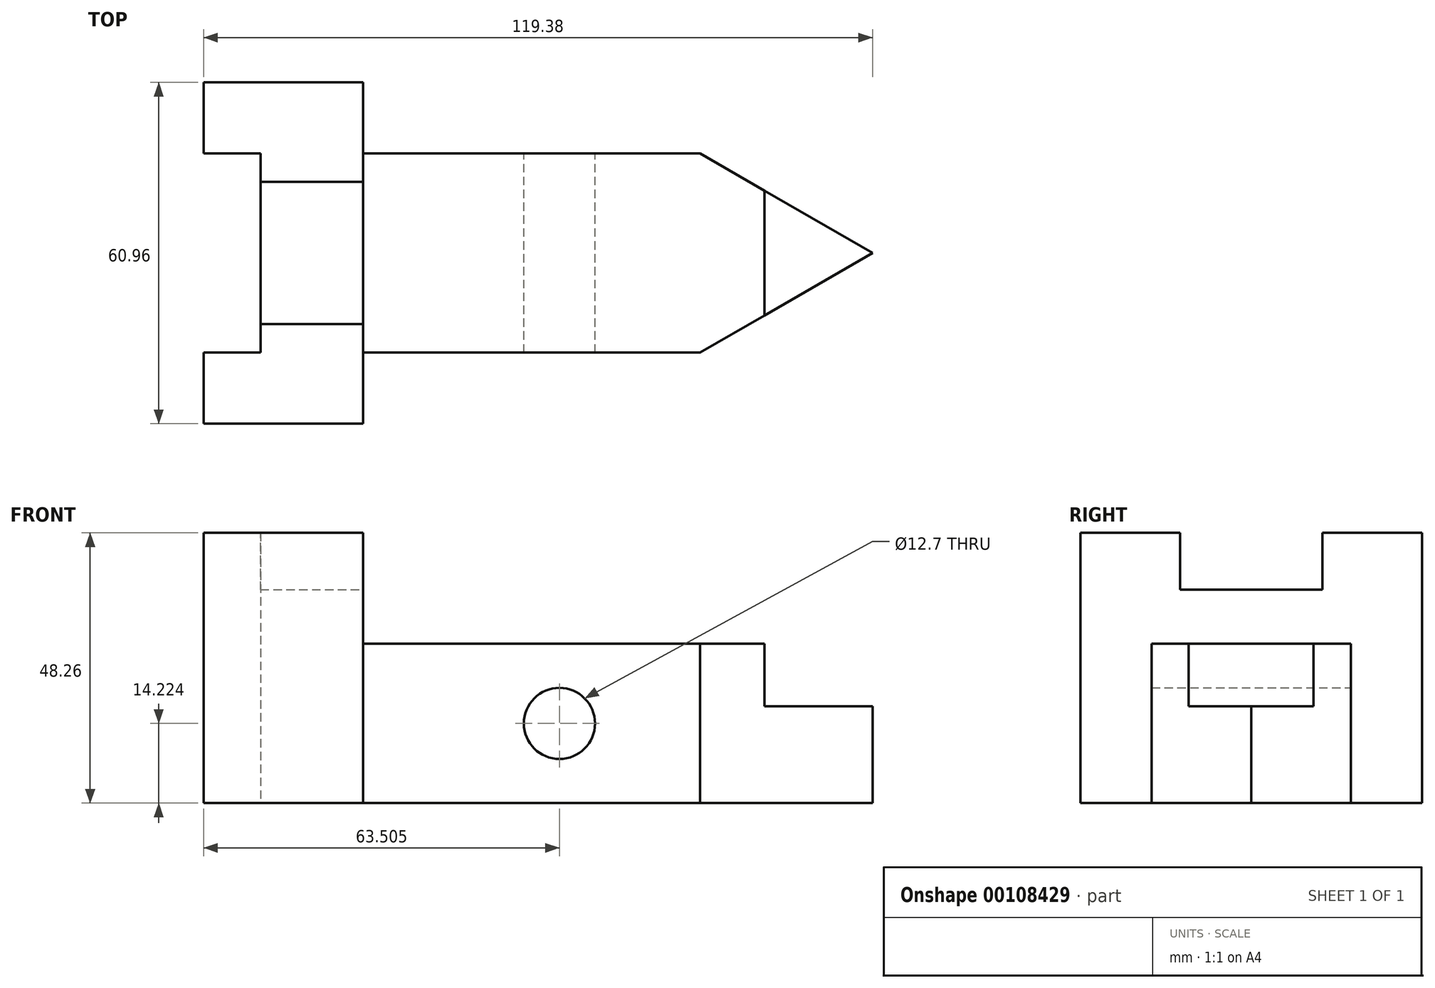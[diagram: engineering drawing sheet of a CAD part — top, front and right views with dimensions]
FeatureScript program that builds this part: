
annotation { "Feature Type Name" : "Feature", "Feature Type Description" : "" }
export const myFeature = defineFeature(function(context is Context, id is Id, definition is map)
    precondition{}
    {
        {
            var Q0;
            Q0=qCreatedBy(makeId("Top.planeOp"),FACE);
            var sketch = newSketch(context, id + "F0", { "sketchPlane" : qUnion([Q0])});
            skLineSegment(sketch, "E0.bottom", {"start": v(-33.19, 31.07) * mm, "end": v(-4.74, 31.07) * mm});
            skLineSegment(sketch, "E0.top", {"start": v(-33.19, -29.9) * mm, "end": v(-4.74, -29.9) * mm});
            skLineSegment(sketch, "E0.right", {"start": v(-4.74, 31.07) * mm, "end": v(-4.74, -29.9) * mm});
            skLineSegment(sketch, "E1", {"start": v(-33.19, 18.37) * mm, "end": v(-23.03, 18.37) * mm});
            skLineSegment(sketch, "E2", {"start": v(-23.03, 18.37) * mm, "end": v(-23.03, -17.2) * mm});
            skLineSegment(sketch, "E3", {"start": v(-23.03, -17.2) * mm, "end": v(-33.19, -17.2) * mm});
            skLineSegment(sketch, "E4", {"start": v(-33.19, 18.37) * mm, "end": v(-33.19, 31.07) * mm});
            skLineSegment(sketch, "E5", {"start": v(-33.19, -17.2) * mm, "end": v(-33.19, -29.9) * mm});
            skSolve(sketch);
        }
        {
            var Q0;
            Q0 = qSketchRegion(id + "F0", true);
            extrude(context, id + "F1", {"entities" : qUnion([Q0]), "depth" : 48.26 * mm});
        }
        {
            var Q0;
            Q0=makeQuery(id+"F1.opExtrude","CAP_FACE",FACE,{"disambiguationData":[OSD([sQuery(id+"F0.wireOp",EDGE,"E0.bottom"),sQuery(id+"F0.wireOp",EDGE,"E0.top"),sQuery(id+"F0.wireOp",EDGE,"E0.right"),sQuery(id+"F0.wireOp",EDGE,"E1"),sQuery(id+"F0.wireOp",EDGE,"E2"),sQuery(id+"F0.wireOp",EDGE,"E3"),sQuery(id+"F0.wireOp",EDGE,"E4"),sQuery(id+"F0.wireOp",EDGE,"E5")])],"isStart":false});
            var sketch = newSketch(context, id + "F2", { "sketchPlane" : qUnion([Q0])});
            skLineSegment(sketch, "E6", {"start": v(-23.03, 13.29) * mm, "end": v(-4.74, 13.29) * mm});
            skLineSegment(sketch, "E7", {"start": v(-4.74, 13.29) * mm, "end": v(-4.74, -12.11) * mm});
            skLineSegment(sketch, "E8", {"start": v(-4.74, -12.11) * mm, "end": v(-23.03, -12.11) * mm});
            skLineSegment(sketch, "E9", {"start": v(-23.03, -12.11) * mm, "end": v(-23.03, 13.29) * mm});
            skSolve(sketch);
        }
        {
            var Q0;
            Q0 = qSketchRegion(id + "F2", true);
            extrude(context, id + "F3", {"entities" : qUnion([Q0]), "operationType" : NewBodyOperationType.REMOVE, "oppositeDirection" : true, "depth" : 10.16 * mm});
        }
        {
            var Q0;
            Q0=qCreatedBy(makeId("Top.planeOp"),FACE);
            var sketch = newSketch(context, id + "F4", { "sketchPlane" : qUnion([Q0])});
            skLineSegment(sketch, "E10.bottom", {"start": v(-4.74, -17.2) * mm, "end": v(55.4, -17.2) * mm});
            skLineSegment(sketch, "E10.top", {"start": v(-4.74, 18.37) * mm, "end": v(55.4, 18.37) * mm});
            skLineSegment(sketch, "E10.left", {"start": v(-4.74, -17.2) * mm, "end": v(-4.74, 18.37) * mm});
            skLineSegment(sketch, "E11", {"start": v(55.4, 18.37) * mm, "end": v(86.2, 0.59) * mm});
            skLineSegment(sketch, "E12", {"start": v(86.2, 0.59) * mm, "end": v(55.4, -17.2) * mm});
            skSolve(sketch);
        }
        {
            var Q0;
            Q0 = qSketchRegion(id + "F4", true);
            extrude(context, id + "F5", {"entities" : qUnion([Q0]), "operationType" : NewBodyOperationType.ADD, "depth" : 28.45 * mm});
        }
        {
            var Q0;
            Q0=qCreatedBy(makeId("Front.planeOp"),FACE);
            var sketch = newSketch(context, id + "F6", { "sketchPlane" : qUnion([Q0])});
            skCircle(sketch, "E13", {"center": v(30.31, 14.22) * mm, "radius": 6.35 * mm});
            skLineSegment(sketch, "E14.bottom", {"start": v(66.9, 17.27) * mm, "end": v(118.64, 17.27) * mm});
            skLineSegment(sketch, "E14.top", {"start": v(66.9, 42.9) * mm, "end": v(118.64, 42.9) * mm});
            skLineSegment(sketch, "E14.left", {"start": v(66.9, 17.27) * mm, "end": v(66.9, 42.9) * mm});
            skLineSegment(sketch, "E14.right", {"start": v(118.64, 17.27) * mm, "end": v(118.64, 42.9) * mm});
            skSolve(sketch);
        }
        {
            var Q0;
            Q0 = qSketchRegion(id + "F6", true);
            extrude(context, id + "F7", {"entities" : qUnion([Q0]), "operationType" : NewBodyOperationType.REMOVE, "endBound" : BoundingType.SYMMETRIC, "depth" : 76.2 * mm});
        }
    });
